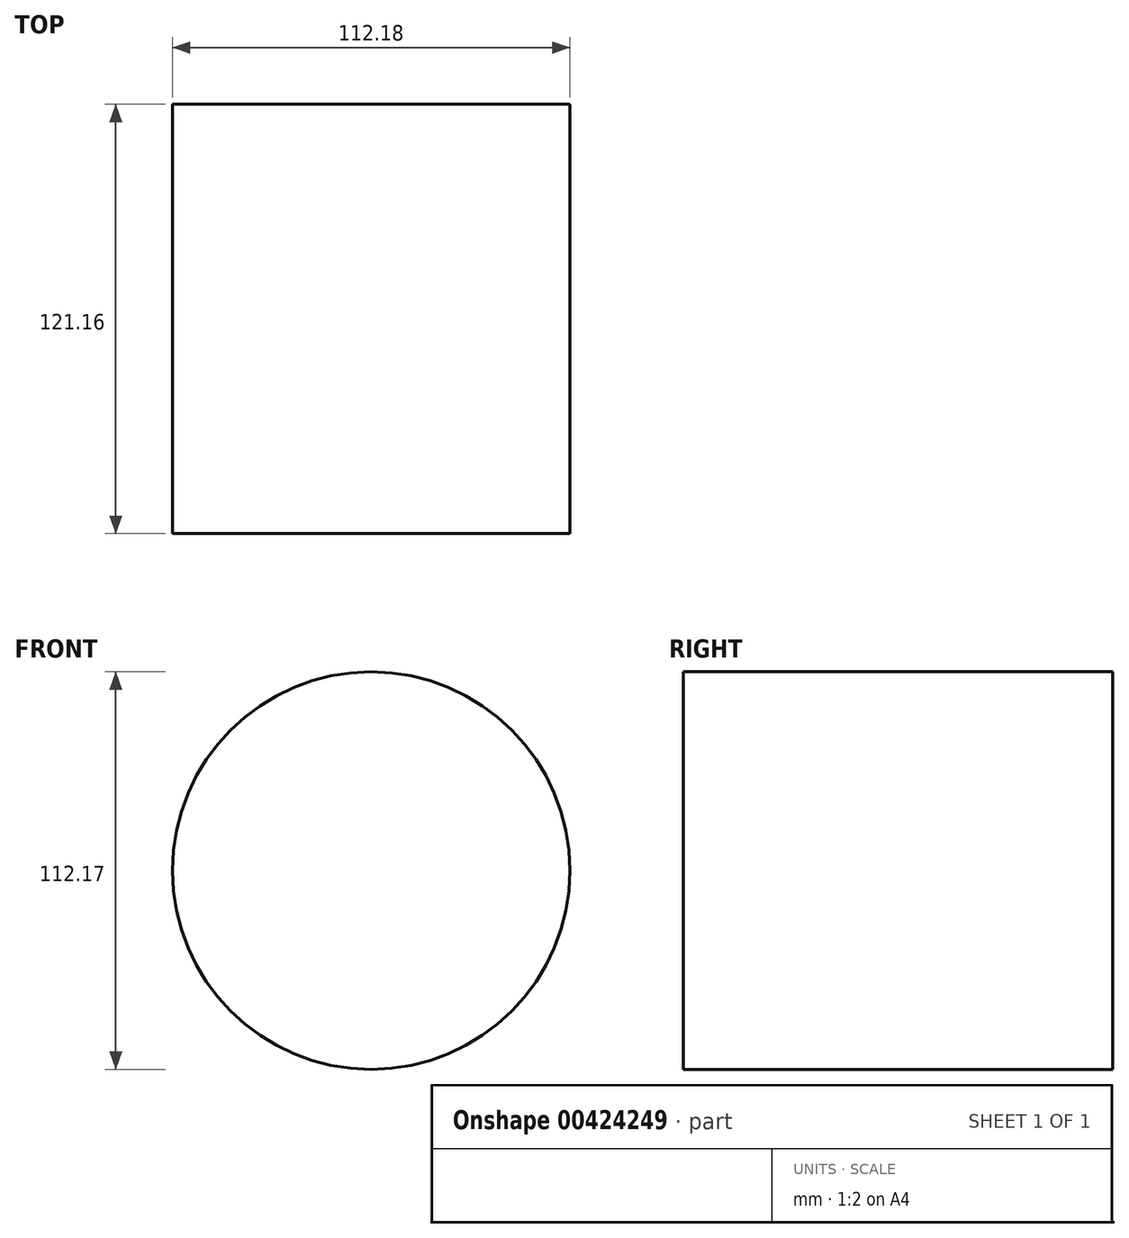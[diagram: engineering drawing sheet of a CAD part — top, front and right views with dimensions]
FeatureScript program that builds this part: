
annotation { "Feature Type Name" : "Feature", "Feature Type Description" : "" }
export const myFeature = defineFeature(function(context is Context, id is Id, definition is map)
    precondition{}
    {
        {
            var Q0;
            Q0=qCreatedBy(makeId("Front.planeOp"),FACE);
            var sketch = newSketch(context, id + "F0", { "sketchPlane" : qUnion([Q0])});
            skCircle(sketch, "E0", {"center": v(-33.83, 31.37) * mm, "radius": 56.09 * mm});
            skSolve(sketch);
        }
        {
            var Q0;
            Q0=makeQuery(id+"F0.imprint","IMPRINT",FACE,{"disambiguationData":[TD([[makeQuery(id+"F0.imprint","IMPRINT",EDGE,{"derivedFrom":sQuery(id+"F0.wireOp",EDGE,"E0")}),1.0]])]});
            extrude(context, id + "F1", {"entities" : qUnion([Q0]), "depth" : 121.16 * mm});
        }
    });
